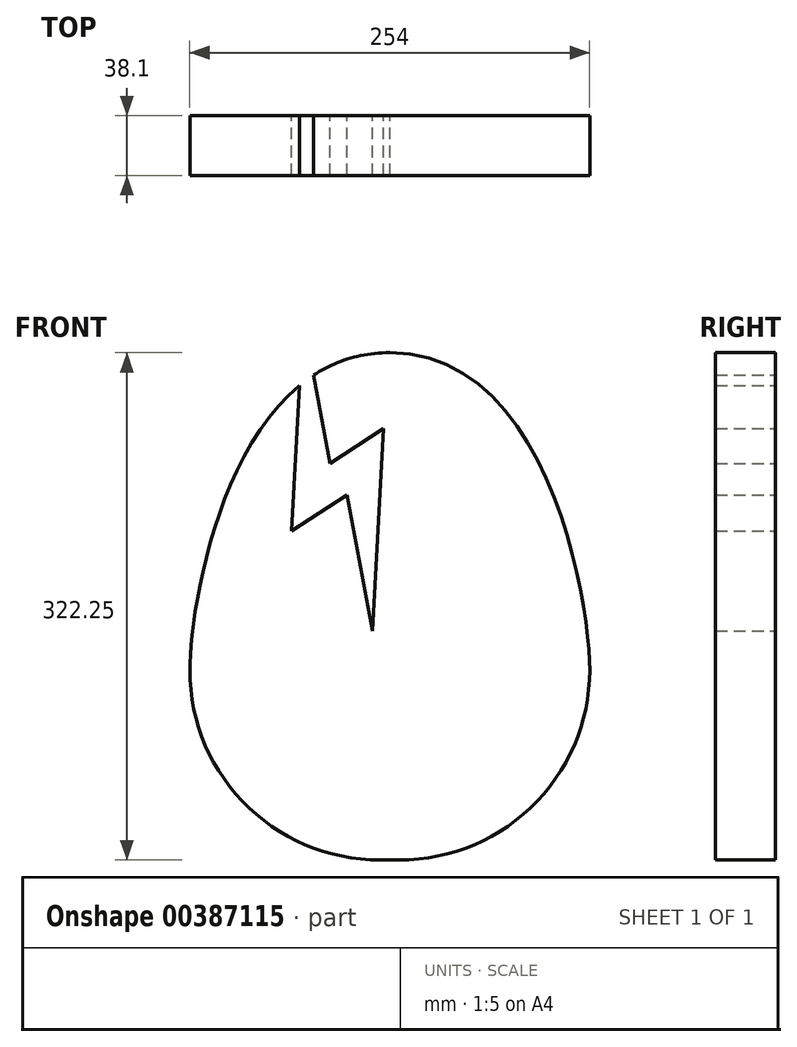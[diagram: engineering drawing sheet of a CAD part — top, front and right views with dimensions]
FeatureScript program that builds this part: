
annotation { "Feature Type Name" : "Feature", "Feature Type Description" : "" }
export const myFeature = defineFeature(function(context is Context, id is Id, definition is map)
    precondition{}
    {
        {
            var Q0;
            Q0=qCreatedBy(makeId("Front.planeOp"),FACE);
            var sketch = newSketch(context, id + "F0", { "sketchPlane" : qUnion([Q0])});
            skArc(sketch, "E0", {"start": v(-124.7, -38.3) * mm, "mid": v(-87.04, -125.73) * mm, "end": v(2.3, -158.6) * mm});
            skFitSpline(sketch, "E1", {"points": [v(-124.7, -38.3) * mm, v(2.3, 163.47) * mm], "startDerivative": vector(0, 122.18) * mm, "endDerivative": vector(306.56, 0) * mm});
            skArc(sketch, "E2.MirrorCS", {"start": v(129.3, -38.3) * mm, "mid": v(91.64, -125.73) * mm, "end": v(2.3, -158.6) * mm});
            skFitSpline(sketch, "E3.MirrorCS", {"points": [v(129.3, -38.3) * mm, v(2.3, 163.47) * mm], "startDerivative": vector(0, 122.18) * mm, "endDerivative": vector(-306.56, 0) * mm});
            skFitSpline(sketch, "E4.MirrorCS", {"points": [v(129.3, -38.3) * mm, v(2.3, 163.47) * mm], "startDerivative": vector(0, 122.18) * mm, "endDerivative": vector(-306.56, 0) * mm});
            skFitSpline(sketch, "E5.MirrorCS", {"points": [v(129.3, -38.3) * mm, v(2.3, 163.47) * mm], "startDerivative": vector(0, 122.18) * mm, "endDerivative": vector(-306.56, 0) * mm});
            skLineSegment(sketch, "E6", {"start": v(-55.12, 142.54) * mm, "end": v(-60.1, 50.15) * mm});
            skLineSegment(sketch, "E7", {"start": v(-60.1, 50.15) * mm, "end": v(-24.94, 73.1) * mm});
            skLineSegment(sketch, "E8", {"start": v(-24.94, 73.1) * mm, "end": v(-8.67, -13.44) * mm});
            skLineSegment(sketch, "E9", {"start": v(-8.67, -13.44) * mm, "end": v(-1.73, 115.2) * mm});
            skLineSegment(sketch, "E10", {"start": v(-1.73, 115.2) * mm, "end": v(-35.7, 93.04) * mm});
            skLineSegment(sketch, "E11", {"start": v(-35.7, 93.04) * mm, "end": v(-46.12, 149.16) * mm});
            skFitSpline(sketch, "E12.trimOffspring", {"points": [v(-124.7, -38.3) * mm, v(2.3, 163.47) * mm], "startDerivative": vector(0, 122.18) * mm, "endDerivative": vector(306.56, 0) * mm});
            skLineSegment(sketch, "E13", {"start": v(-124.7, -38.3) * mm, "end": v(129.3, -38.3) * mm, "construction": true});
            skLineSegment(sketch, "E14", {"start": v(2.3, -158.6) * mm, "end": v(2.3, -38.18) * mm, "construction": true});
            skSolve(sketch);
        }
        {
            var Q0;
            Q0=makeQuery(id+"F0.imprint","IMPRINT",FACE,{"disambiguationData":[TD([[makeQuery(id+"F0.imprint","IMPRINT",EDGE,{"derivedFrom":sQuery(id+"F0.wireOp",EDGE,"E0")}),1.0]])]});
            extrude(context, id + "F1", {"entities" : qUnion([Q0]), "depth" : 38.1 * mm});
        }
    });
